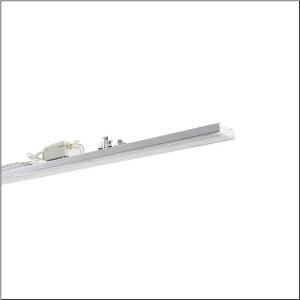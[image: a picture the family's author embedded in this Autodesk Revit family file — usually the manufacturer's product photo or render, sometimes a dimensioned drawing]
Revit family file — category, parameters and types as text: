
# Revit family: licross_11_recessed_ho_51tl11mv4hxs
name_source: partatom
category: Lighting Fixtures
units: mm (PartAtom-declared; Revit-internal decimal feet)

## family parameters
Cut with Voids When Loaded = No
Host = Face
Light Source = No
Part Type = Normal
Room Calculation Point = No
Round Connector Dimension = Use Diameter
Shared = No

## types (1)
- --- (1 x LED, 17230 lm, 89.2 W, 4000K)
    Apparent Load = 89 VA
    CIE Flux Codes = 87 95 99 100 100
    Color Rendering = 80
    Color Temperature = 4000K
    Default Elevation = 1800 mm
    Description = Licross 11 Recessed HO, luminaire insert, of sheet steel, coil coated, white, length: 2.250mm, width: 66mm, height: 67mm, LED rated luminous flux: 17.230lm, light colour: 840, SDCM (Standard Deviation of Colour Matching)MacAdam ≤ 2 SDCM (initial), control gear: ON/OFF Multilumen, with plug, 3-pole, with phase selection, mains connection: 220..240V, AC, 50/60Hz, rated input power: 89W, internal wiring halogen-free, primary light control with lens, of plastic, primary optical cover: cover, of PMMA, light emission: direct distribution, primary light characteristic: symmetric, protection rating (complete): IP40, insulation class (complete): insulation class I (protective earthing), certification: CE, ENEC, VDE, UKCA, protection symbol: D if used in an environment without relevant dust loads with corresponding accessories, impact resistance: IK06, permissible ambient temperature for indoor applications: -35..+35°C, corresponds to IFS (International Featured Standards) requirements for safety and quality in the food industry, reducing of maximum allowable ambient temperature of 5°C with ceiling mounting, The light source and the operating device comply with the requirements of the Ecodesign Regulation (EU) 2019/2020 and are replaceable in accordance with this regulation, packaging unit: 1 piece
    Height = 58 mm
    Lamp = 1 x LED
    Lamp Light Flux = 17230 lm
    Lamp Power = 89.2 W
    Lamp count = 1
    Length = 2250 mm
    Luminous efficacy = 193 lm/W
    Manufacturer = Siteco
    ModVariant = No
    Model = 51TL11MV4HXS
    Mounting Place = Ceiling
    Mounting Type = Pendant
    Number of Poles = 1
    OnlyDefault = Yes
    Power Factor = 1
    Product Name = Licross 11 Recessed HO
    Product group = luminaire insert | ceiling pendant
    ProductGroupID = 901
    Protection Class = Protection class I
    Protection Degree = IP 40
    RLX_Detail_Level = 1
    RLX_Emergency_Light_Flux = 0 lm
    RLX_Emergency_Type = 0
    RLX_Emergency_Type_DB = No
    RlxData = <blob elided: 27201 chars, md5=b4542c66>
    Socket = socket
    Standby Power = 0 W
    System Light Flux = 17230 lm
    System Power = 89 W
    Type Comments = factory setting: luminous flux: 100 % | (A | C | E) | 210 mA
    Type Image = l_1296930.jpg
    URL = http://relux.com
    VarID = @adj_091023
    Voltage = 0 V
    Weight = 0.00 kg
    Width = 66 mm

## geometry (parser evidence)
native form markers: Blend x4, Sweep x11
no freeform markers — native parametric forms only
